# Revit family: Wire_Basket-Grohe-40664000
name_source: partatom
category: Specialty Equipment
revit_build: Autodesk Revit 2018 (Build: 20170223_1515(x64)
units: mm (PartAtom-declared; Revit-internal decimal feet)

## family parameters
Always vertical = No
Cut with Voids When Loaded = No
OmniClass Number = 23.40.20.21.34
OmniClass Title = Soap Holders, Dispensers
Part Type = Normal
Room Calculation Point = No
Round Connector Dimension = Use Diameter
Shared = Yes
Work Plane-Based = Yes

## types (1)
- 40664000
    Assembly Code = C1030200
    Body Material = Metal-Grohe-000-Starlight Chrome
    Default Elevation = 0"
    Description = Filing Basket
    Height = 1 11/32"
    Installation Type = Angle Wall Mounted
    Length = 5 7/8"
    Manufacturer = Grohe
    Material = Metal-Grohe-000-Starlight Chrome
    Model = 40664000
    Price = Prices may vary. Please consult Manufacturer Representative for most up-to-date price list.
    Product Documentation Link = https://americanstandard.box.com
    Product Page URL = https://www.grohe.ca
    Region = North America
    URL = https://www.grohe.ca
    Warranty Information = Limited Lifetime warranty
    Width = 8"

## geometry (parser evidence)
native form markers: Sweep x2
no freeform markers — native parametric forms only
